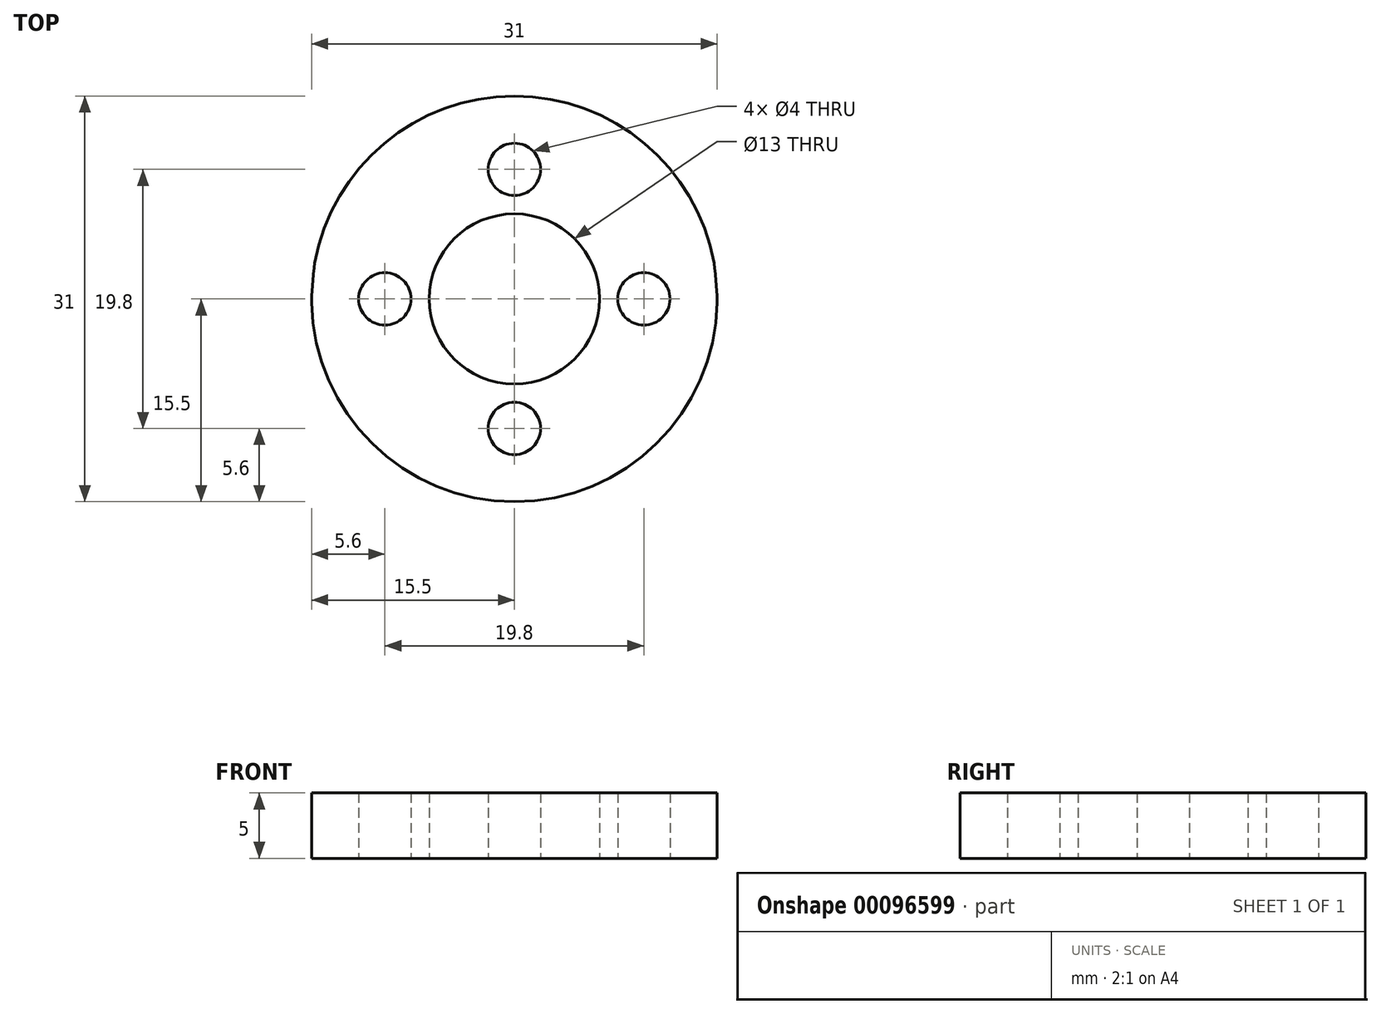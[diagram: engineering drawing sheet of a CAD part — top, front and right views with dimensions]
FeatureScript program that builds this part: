
annotation { "Feature Type Name" : "Feature", "Feature Type Description" : "" }
export const myFeature = defineFeature(function(context is Context, id is Id, definition is map)
    precondition{}
    {
        {
            var Q0;
            Q0=qCreatedBy(makeId("Top.planeOp"),FACE);
            var sketch = newSketch(context, id + "F0", { "sketchPlane" : qUnion([Q0])});
            skCircle(sketch, "E0", {"center": v(0, 0) * mm, "radius": 6.5 * mm});
            skLineSegment(sketch, "E1", {"start": v(0, 0) * mm, "end": v(0, 9.9) * mm, "construction": true});
            skCircle(sketch, "E2", {"center": v(0, 9.9) * mm, "radius": 2 * mm});
            skCircle(sketch, "E3.1.0", {"center": v(-9.9, 0) * mm, "radius": 2 * mm});
            skCircle(sketch, "E3.2.0", {"center": v(0, -9.9) * mm, "radius": 2 * mm});
            skCircle(sketch, "E3.3.0", {"center": v(9.9, 0) * mm, "radius": 2 * mm});
            skCircle(sketch, "E4", {"center": v(0, 0) * mm, "radius": 15.5 * mm});
            skLineSegment(sketch, "E5", {"start": v(-15.5, 0) * mm, "end": v(-9.46, 75.4) * mm});
            skLineSegment(sketch, "E6", {"start": v(15.5, 0) * mm, "end": v(9.44, 75.76) * mm});
            skLineSegment(sketch, "E7", {"start": v(0, 0) * mm, "end": v(0, 75) * mm, "construction": true});
            skArc(sketch, "E8", {"start": v(9.44, 75.76) * mm, "mid": v(-0.18, 84.47) * mm, "end": v(-9.46, 75.4) * mm});
            skLineSegment(sketch, "E9.bottom", {"start": v(6.35, 28.58) * mm, "end": v(-6.35, 28.58) * mm});
            skLineSegment(sketch, "E9.top", {"start": v(6.35, 73.03) * mm, "end": v(-6.35, 73.03) * mm});
            skLineSegment(sketch, "E9.left", {"start": v(6.35, 28.58) * mm, "end": v(6.35, 73.03) * mm});
            skLineSegment(sketch, "E9.right", {"start": v(-6.35, 28.58) * mm, "end": v(-6.35, 73.03) * mm});
            skPoint(sketch, "E9.middle", {"position": v(0, 50.8) * mm});
            skLineSegment(sketch, "E10.bottom", {"start": v(3.17, 28.58) * mm, "end": v(-3.18, 28.58) * mm});
            skLineSegment(sketch, "E10.top", {"start": v(3.17, 73.03) * mm, "end": v(-3.18, 73.03) * mm});
            skLineSegment(sketch, "E10.left", {"start": v(3.17, 28.58) * mm, "end": v(3.17, 73.03) * mm});
            skLineSegment(sketch, "E10.right", {"start": v(-3.18, 28.58) * mm, "end": v(-3.18, 73.03) * mm});
            skCircle(sketch, "E11", {"center": v(0, 0) * mm, "radius": 9.9 * mm, "construction": true});
            skLineSegment(sketch, "E12", {"start": v(-13.21, 28.58) * mm, "end": v(-9.46, 28.58) * mm});
            skLineSegment(sketch, "E13", {"start": v(-9.46, 28.58) * mm, "end": v(-9.46, 75.4) * mm});
            skLineSegment(sketch, "E14", {"start": v(9.44, 75.76) * mm, "end": v(9.44, 28.58) * mm});
            skLineSegment(sketch, "E15", {"start": v(9.44, 28.58) * mm, "end": v(13.22, 28.58) * mm});
            skSolve(sketch);
        }
        {
            var Q0;
            {var subQ13=sQuery(id+"F0.wireOp",EDGE,"E8");Q0=makeQuery(id+"F0.imprint","IMPRINT",FACE,{"disambiguationData":[TD([[makeQuery(id+"F0.imprint","IMPRINT",EDGE,{"derivedFrom":subQ13}),1.0]])]});}
            var Q1;
            Q1=makeQuery(id+"F0.imprint","IMPRINT",FACE,{"disambiguationData":[TD([[makeQuery(id+"F0.imprint","IMPRINT",EDGE,{"derivedFrom":sQuery(id+"F0.wireOp",EDGE,"E0")}),-1.0]])]});
            var Q2;
            Q2=makeQuery(id+"F0.imprint","IMPRINT",FACE,{"disambiguationData":[TD([[makeQuery(id+"F0.imprint","IMPRINT",EDGE,{"derivedFrom":sQuery(id+"F0.wireOp",EDGE,"E10.bottom")}),-1.0]])]});
            extrude(context, id + "F1", {"entities" : qUnion([Q0, Q1, Q2]), "depth" : 5 * mm, "offsetDistance" : 25.4 * mm});
        }
        {
            var Q0;
            Q0=makeQuery(id+"F1.opExtrude","SWEPT_EDGE",EDGE,{"disambiguationData":[OSD([sQuery(id+"F0.wireOp",EDGE,"E6"),sQuery(id+"F0.wireOp",EDGE,"E15")])]});
            var Q1;
            Q1=makeQuery(id+"F1.opExtrude","SWEPT_EDGE",EDGE,{"disambiguationData":[OSD([sQuery(id+"F0.wireOp",EDGE,"E5"),sQuery(id+"F0.wireOp",EDGE,"E12")])]});
            fillet(context, id + "F2", {"entities" : qUnion([Q0, Q1]), "radius" : 5.08 * mm, "tangentPropagation" : true, "allowEdgeOverflow" : false});
        }
    });
